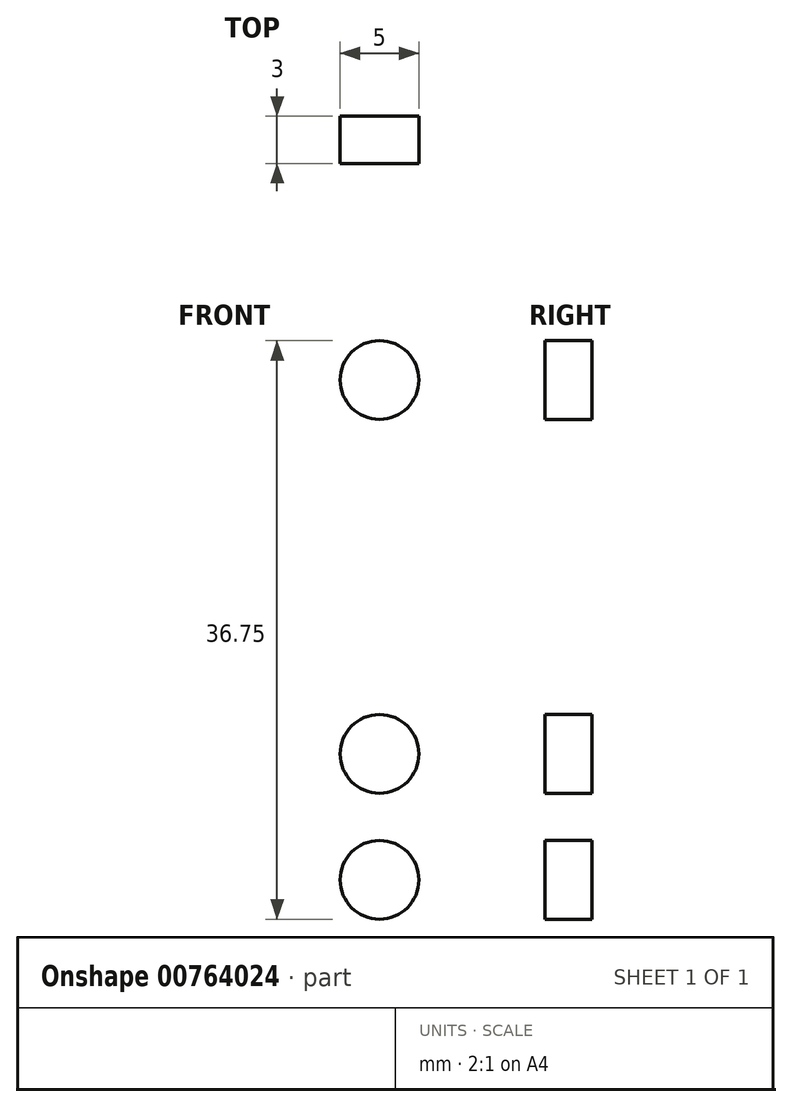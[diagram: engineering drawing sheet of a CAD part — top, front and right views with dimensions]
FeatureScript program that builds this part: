
annotation { "Feature Type Name" : "Feature", "Feature Type Description" : "" }
export const myFeature = defineFeature(function(context is Context, id is Id, definition is map)
    precondition{}
    {
        {
            var Q0;
            Q0=qCreatedBy(makeId("Front.planeOp"),FACE);
            var sketch = newSketch(context, id + "F0", { "sketchPlane" : qUnion([Q0])});
            skLineSegment(sketch, "E0.bottom", {"start": v(-8, 32) * mm, "end": v(8, 32) * mm});
            skLineSegment(sketch, "E0.top", {"start": v(-8, -32) * mm, "end": v(8, -32) * mm});
            skLineSegment(sketch, "E0.left", {"start": v(-8, 32) * mm, "end": v(-8, -32) * mm});
            skLineSegment(sketch, "E0.right", {"start": v(8, 32) * mm, "end": v(8, -32) * mm});
            skPoint(sketch, "E0.middle", {"position": v(0, 0) * mm});
            skSolve(sketch);
        }
        {
            var Q0;
            Q0=makeQuery(id+"F0.imprint","IMPRINT",FACE,{"disambiguationData":[TD([[makeQuery(id+"F0.imprint","IMPRINT",EDGE,{"derivedFrom":sQuery(id+"F0.wireOp",EDGE,"E0.bottom")}),-1.0]])]});
            extrude(context, id + "F1", {"entities" : qUnion([Q0]), "depth" : 3 * mm, "offsetDistance" : 25 * mm});
        }
        {
            var Q0;
            Q0=makeQuery(id+"F1.opExtrude","CAP_FACE",FACE,{"disambiguationData":[OSD([sQuery(id+"F0.wireOp",EDGE,"E0.bottom"),sQuery(id+"F0.wireOp",EDGE,"E0.top"),sQuery(id+"F0.wireOp",EDGE,"E0.left"),sQuery(id+"F0.wireOp",EDGE,"E0.right")])],"isStart":false});
            var sketch = newSketch(context, id + "F2", { "sketchPlane" : qUnion([Q0])});
            skLineSegment(sketch, "E1", {"start": v(0, 32) * mm, "end": v(0, -32) * mm});
            skCircle(sketch, "E2", {"center": v(0, -23.75) * mm, "radius": 2.5 * mm});
            skCircle(sketch, "E3", {"center": v(0, -15.75) * mm, "radius": 2.5 * mm});
            skCircle(sketch, "E4", {"center": v(0, -7.75) * mm, "radius": 2.5 * mm});
            skCircle(sketch, "E5", {"center": v(0, 0) * mm, "radius": 2.5 * mm});
            skCircle(sketch, "E6", {"center": v(0, 8) * mm, "radius": 2.5 * mm});
            skCircle(sketch, "E7", {"center": v(0, 16) * mm, "radius": 2.5 * mm});
            skCircle(sketch, "E8", {"center": v(0, 24) * mm, "radius": 2.5 * mm});
            skSolve(sketch);
        }
        {
            var Q0;
            Q0=makeQuery(id+"F1.opExtrude","CAP_FACE",FACE,{"disambiguationData":[OSD([sQuery(id+"F0.wireOp",EDGE,"E0.bottom"),sQuery(id+"F0.wireOp",EDGE,"E0.top"),sQuery(id+"F0.wireOp",EDGE,"E0.left"),sQuery(id+"F0.wireOp",EDGE,"E0.right")])],"isStart":false});
            var sketch = newSketch(context, id + "F3", { "sketchPlane" : qUnion([Q0])});
            skCircle(sketch, "E9", {"center": v(0, 23.5) * mm, "radius": 2.5 * mm});
            skCircle(sketch, "E10", {"center": v(0, 15.5) * mm, "radius": 2.5 * mm});
            skCircle(sketch, "E11", {"center": v(0, 7.5) * mm, "radius": 2.5 * mm});
            skCircle(sketch, "E12", {"center": v(0, 0) * mm, "radius": 2.5 * mm});
            skCircle(sketch, "E13", {"center": v(0, -8) * mm, "radius": 2.5 * mm});
            skCircle(sketch, "E14", {"center": v(0, -16) * mm, "radius": 2.5 * mm});
            skCircle(sketch, "E15", {"center": v(0, -25.9) * mm, "radius": 2.5 * mm});
            skSolve(sketch);
        }
        {
            var Q0;
            {var subQ0=sQuery(id+"F2.wireOp",EDGE,"E8");var subQ1=sQuery(id+"F2.wireOp",EDGE,"E1");var subQ2=makeQuery(id+"F2.imprint","INTERSECT",VERTEX,{"disambiguationData":[OD(0.0)],"derivedFrom":[subQ1,subQ0]});Q0=makeQuery(id+"F2.imprint","IMPRINT",FACE,{"disambiguationData":[TD([[makeQuery(id+"F2.imprint","IMPRINT",EDGE,{"disambiguationData":[TD([[subQ2,-1.0]])],"derivedFrom":subQ1}),1.0]])]});}
            var Q1;
            {var subQ0=sQuery(id+"F2.wireOp",EDGE,"E8");var subQ1=sQuery(id+"F2.wireOp",EDGE,"E1");var subQ2=makeQuery(id+"F2.imprint","INTERSECT",VERTEX,{"disambiguationData":[OD(0.0)],"derivedFrom":[subQ1,subQ0]});Q1=makeQuery(id+"F2.imprint","IMPRINT",FACE,{"disambiguationData":[TD([[makeQuery(id+"F2.imprint","IMPRINT",EDGE,{"disambiguationData":[TD([[subQ2,-1.0]])],"derivedFrom":subQ1}),-1.0]])]});}
            var Q2;
            {var subQ0=sQuery(id+"F2.wireOp",EDGE,"E7");var subQ1=sQuery(id+"F2.wireOp",EDGE,"E1");var subQ2=makeQuery(id+"F2.imprint","INTERSECT",VERTEX,{"disambiguationData":[OD(0.0)],"derivedFrom":[subQ1,subQ0]});Q2=makeQuery(id+"F2.imprint","IMPRINT",FACE,{"disambiguationData":[TD([[makeQuery(id+"F2.imprint","IMPRINT",EDGE,{"disambiguationData":[TD([[subQ2,-1.0]])],"derivedFrom":subQ1}),1.0]])]});}
            var Q3;
            {var subQ0=sQuery(id+"F2.wireOp",EDGE,"E7");var subQ1=sQuery(id+"F2.wireOp",EDGE,"E1");var subQ2=makeQuery(id+"F2.imprint","INTERSECT",VERTEX,{"disambiguationData":[OD(0.0)],"derivedFrom":[subQ1,subQ0]});Q3=makeQuery(id+"F2.imprint","IMPRINT",FACE,{"disambiguationData":[TD([[makeQuery(id+"F2.imprint","IMPRINT",EDGE,{"disambiguationData":[TD([[subQ2,-1.0]])],"derivedFrom":subQ1}),-1.0]])]});}
            var Q4;
            {var subQ0=sQuery(id+"F2.wireOp",EDGE,"E6");var subQ1=sQuery(id+"F2.wireOp",EDGE,"E1");var subQ2=makeQuery(id+"F2.imprint","INTERSECT",VERTEX,{"disambiguationData":[OD(0.0)],"derivedFrom":[subQ1,subQ0]});Q4=makeQuery(id+"F2.imprint","IMPRINT",FACE,{"disambiguationData":[TD([[makeQuery(id+"F2.imprint","IMPRINT",EDGE,{"disambiguationData":[TD([[subQ2,-1.0]])],"derivedFrom":subQ1}),1.0]])]});}
            var Q5;
            {var subQ0=sQuery(id+"F2.wireOp",EDGE,"E6");var subQ1=sQuery(id+"F2.wireOp",EDGE,"E1");var subQ2=makeQuery(id+"F2.imprint","INTERSECT",VERTEX,{"disambiguationData":[OD(0.0)],"derivedFrom":[subQ1,subQ0]});Q5=makeQuery(id+"F2.imprint","IMPRINT",FACE,{"disambiguationData":[TD([[makeQuery(id+"F2.imprint","IMPRINT",EDGE,{"disambiguationData":[TD([[subQ2,-1.0]])],"derivedFrom":subQ1}),-1.0]])]});}
            var Q6;
            {var subQ0=sQuery(id+"F2.wireOp",EDGE,"E5");var subQ1=sQuery(id+"F2.wireOp",EDGE,"E1");var subQ2=makeQuery(id+"F2.imprint","INTERSECT",VERTEX,{"disambiguationData":[OD(0.0)],"derivedFrom":[subQ1,subQ0]});Q6=makeQuery(id+"F2.imprint","IMPRINT",FACE,{"disambiguationData":[TD([[makeQuery(id+"F2.imprint","IMPRINT",EDGE,{"disambiguationData":[TD([[subQ2,-1.0]])],"derivedFrom":subQ1}),1.0]])]});}
            var Q7;
            {var subQ0=sQuery(id+"F2.wireOp",EDGE,"E5");var subQ1=sQuery(id+"F2.wireOp",EDGE,"E1");var subQ2=makeQuery(id+"F2.imprint","INTERSECT",VERTEX,{"disambiguationData":[OD(0.0)],"derivedFrom":[subQ1,subQ0]});Q7=makeQuery(id+"F2.imprint","IMPRINT",FACE,{"disambiguationData":[TD([[makeQuery(id+"F2.imprint","IMPRINT",EDGE,{"disambiguationData":[TD([[subQ2,-1.0]])],"derivedFrom":subQ1}),-1.0]])]});}
            var Q8;
            {var subQ0=sQuery(id+"F2.wireOp",EDGE,"E4");var subQ1=sQuery(id+"F2.wireOp",EDGE,"E1");var subQ2=makeQuery(id+"F2.imprint","INTERSECT",VERTEX,{"disambiguationData":[OD(0.0)],"derivedFrom":[subQ1,subQ0]});Q8=makeQuery(id+"F2.imprint","IMPRINT",FACE,{"disambiguationData":[TD([[makeQuery(id+"F2.imprint","IMPRINT",EDGE,{"disambiguationData":[TD([[subQ2,-1.0]])],"derivedFrom":subQ1}),1.0]])]});}
            var Q9;
            {var subQ0=sQuery(id+"F2.wireOp",EDGE,"E4");var subQ1=sQuery(id+"F2.wireOp",EDGE,"E1");var subQ2=makeQuery(id+"F2.imprint","INTERSECT",VERTEX,{"disambiguationData":[OD(0.0)],"derivedFrom":[subQ1,subQ0]});Q9=makeQuery(id+"F2.imprint","IMPRINT",FACE,{"disambiguationData":[TD([[makeQuery(id+"F2.imprint","IMPRINT",EDGE,{"disambiguationData":[TD([[subQ2,-1.0]])],"derivedFrom":subQ1}),-1.0]])]});}
            var Q10;
            {var subQ0=sQuery(id+"F2.wireOp",EDGE,"E3");var subQ1=sQuery(id+"F2.wireOp",EDGE,"E1");var subQ2=makeQuery(id+"F2.imprint","INTERSECT",VERTEX,{"disambiguationData":[OD(0.0)],"derivedFrom":[subQ1,subQ0]});Q10=makeQuery(id+"F2.imprint","IMPRINT",FACE,{"disambiguationData":[TD([[makeQuery(id+"F2.imprint","IMPRINT",EDGE,{"disambiguationData":[TD([[subQ2,-1.0]])],"derivedFrom":subQ1}),1.0]])]});}
            var Q11;
            {var subQ0=sQuery(id+"F2.wireOp",EDGE,"E3");var subQ1=sQuery(id+"F2.wireOp",EDGE,"E1");var subQ2=makeQuery(id+"F2.imprint","INTERSECT",VERTEX,{"disambiguationData":[OD(0.0)],"derivedFrom":[subQ1,subQ0]});Q11=makeQuery(id+"F2.imprint","IMPRINT",FACE,{"disambiguationData":[TD([[makeQuery(id+"F2.imprint","IMPRINT",EDGE,{"disambiguationData":[TD([[subQ2,-1.0]])],"derivedFrom":subQ1}),-1.0]])]});}
            var Q12;
            {var subQ0=sQuery(id+"F2.wireOp",EDGE,"E2");var subQ1=sQuery(id+"F2.wireOp",EDGE,"E1");var subQ2=makeQuery(id+"F2.imprint","INTERSECT",VERTEX,{"disambiguationData":[OD(0.0)],"derivedFrom":[subQ1,subQ0]});Q12=makeQuery(id+"F2.imprint","IMPRINT",FACE,{"disambiguationData":[TD([[makeQuery(id+"F2.imprint","IMPRINT",EDGE,{"disambiguationData":[TD([[subQ2,-1.0]])],"derivedFrom":subQ1}),1.0]])]});}
            var Q13;
            {var subQ0=sQuery(id+"F2.wireOp",EDGE,"E2");var subQ1=sQuery(id+"F2.wireOp",EDGE,"E1");var subQ2=makeQuery(id+"F2.imprint","INTERSECT",VERTEX,{"disambiguationData":[OD(0.0)],"derivedFrom":[subQ1,subQ0]});Q13=makeQuery(id+"F2.imprint","IMPRINT",FACE,{"disambiguationData":[TD([[makeQuery(id+"F2.imprint","IMPRINT",EDGE,{"disambiguationData":[TD([[subQ2,-1.0]])],"derivedFrom":subQ1}),-1.0]])]});}
            extrude(context, id + "F4", {"entities" : qUnion([Q0, Q1, Q2, Q3, Q4, Q5, Q6, Q7, Q8, Q9, Q10, Q11, Q12, Q13]), "operationType" : NewBodyOperationType.REMOVE, "endBound" : BoundingType.THROUGH_ALL, "oppositeDirection" : true, "depth" : 25 * mm, "offsetDistance" : 25 * mm});
        }
    });
